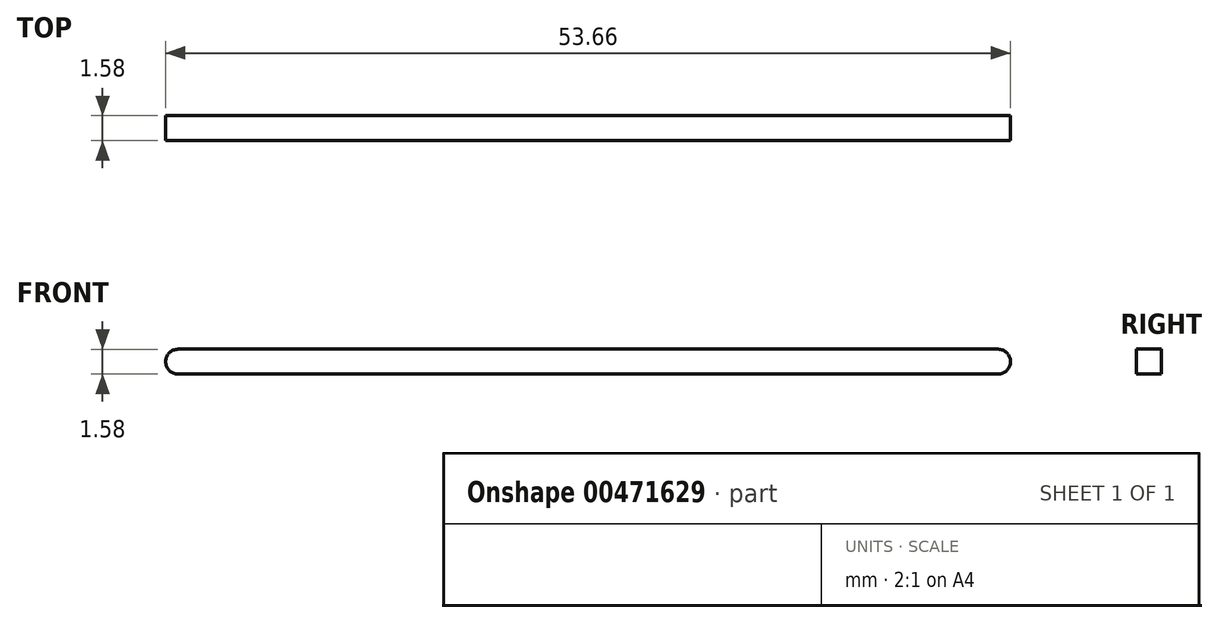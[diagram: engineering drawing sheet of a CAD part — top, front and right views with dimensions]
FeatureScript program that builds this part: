
annotation { "Feature Type Name" : "Feature", "Feature Type Description" : "" }
export const myFeature = defineFeature(function(context is Context, id is Id, definition is map)
    precondition{}
    {
        {
            var Q0;
            Q0=qCreatedBy(makeId("Front.planeOp"),FACE);
            var sketch = newSketch(context, id + "F0", { "sketchPlane" : qUnion([Q0])});
            skLineSegment(sketch, "E0.bottom", {"start": v(26.04, -0.8) * mm, "end": v(-26.04, -0.8) * mm});
            skLineSegment(sketch, "E0.top", {"start": v(26.03, 0.8) * mm, "end": v(-26.03, 0.8) * mm});
            skLineSegment(sketch, "E0.left", {"start": v(26.04, -0.8) * mm, "end": v(26.04, 0.8) * mm});
            skLineSegment(sketch, "E0.right", {"start": v(-26.04, -0.8) * mm, "end": v(-26.04, 0.8) * mm});
            skPoint(sketch, "E0.middle", {"position": v(0, 0) * mm});
            skCircle(sketch, "E1", {"center": v(-26.04, 0) * mm, "radius": 0.8 * mm});
            skCircle(sketch, "E2", {"center": v(26.04, 0) * mm, "radius": 0.8 * mm});
            skSolve(sketch);
        }
        {
            var Q0;
            {var subQ0=sQuery(id+"F0.wireOp",EDGE,"E0.bottom");Q0=makeQuery(id+"F0.imprint","IMPRINT",FACE,{"disambiguationData":[TD([[makeQuery(id+"F0.imprint","IMPRINT",EDGE,{"derivedFrom":subQ0}),-1.0]])]});}
            var Q1;
            {var subQ0=sQuery(id+"F0.wireOp",EDGE,"E0.right");Q1=makeQuery(id+"F0.imprint","IMPRINT",FACE,{"disambiguationData":[TD([[makeQuery(id+"F0.imprint","IMPRINT",EDGE,{"derivedFrom":subQ0}),-1.0]])]});}
            var Q2;
            {var subQ0=sQuery(id+"F0.wireOp",EDGE,"E0.right");Q2=makeQuery(id+"F0.imprint","IMPRINT",FACE,{"disambiguationData":[TD([[makeQuery(id+"F0.imprint","IMPRINT",EDGE,{"derivedFrom":subQ0}),1.0]])]});}
            var Q3;
            {var subQ0=sQuery(id+"F0.wireOp",EDGE,"E0.left");Q3=makeQuery(id+"F0.imprint","IMPRINT",FACE,{"disambiguationData":[TD([[makeQuery(id+"F0.imprint","IMPRINT",EDGE,{"derivedFrom":subQ0}),1.0]])]});}
            var Q4;
            {var subQ0=sQuery(id+"F0.wireOp",EDGE,"E0.left");Q4=makeQuery(id+"F0.imprint","IMPRINT",FACE,{"disambiguationData":[TD([[makeQuery(id+"F0.imprint","IMPRINT",EDGE,{"derivedFrom":subQ0}),-1.0]])]});}
            extrude(context, id + "F1", {"entities" : qUnion([Q0, Q1, Q2, Q3, Q4]), "depth" : 1.59 * mm, "symmetric" : true});
        }
    });
